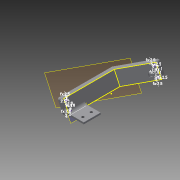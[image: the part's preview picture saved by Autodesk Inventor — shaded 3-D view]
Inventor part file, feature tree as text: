
AUTODESK INVENTOR PART (.ipt)
format: ipt  version: 2014 SP2 (Build 180247200, 247)  size: 199,680 bytes
history: native  units: mm
features: sketch x6, extrude x5, other x2, fillet x2, shell x1, projected_geometry x1
ambient origin geometry x8: Origin, YZ Plane, XZ Plane, XY Plane, X Axis, Y Axis, Z Axis, Center Point
bodies: Body1 (feature_tree)
feature tree (17):
  extrude  "押し出し10"  Depth=3.0mm
  other  "作業平面3"
  extrude  "押し出し11"  Depth=3.0mm
  other  "作業平面4"
  extrude  "押し出し14"  Depth=10.0mm
  extrude  "押し出し15"  Depth=18.0mm
  sketch  "スケッチ21"
  sketch  "スケッチ22"
  fillet  "フィレット4"  Radius=5.0mm
  shell  "シェル2"  Thickness=6.0mm
  extrude  "押し出し16"  Depth=20.0mm
  fillet  "フィレット5"  Radius=2.0mm
  sketch  "スケッチ14"
  sketch  "スケッチ19"
  projected_geometry  "投影ループ5"
  sketch  "スケッチ20"
  sketch  "スケッチ23"
